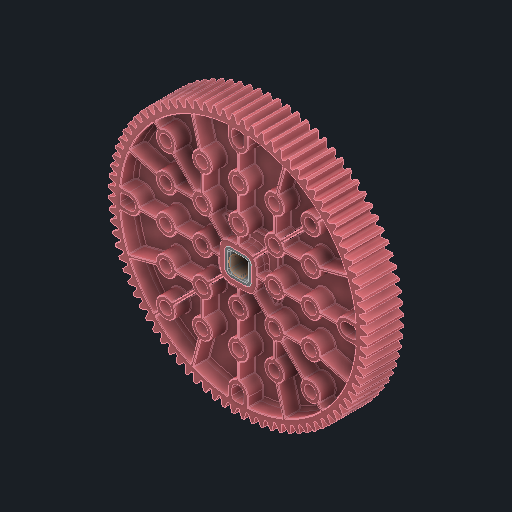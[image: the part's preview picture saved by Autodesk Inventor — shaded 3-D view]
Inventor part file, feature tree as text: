
AUTODESK INVENTOR PART (.ipt)
format: ipt  version: 2024 (Build 280153000, 153)  size: 5,321,216 bytes
history: native  units: in
note: dims shown in document units (in); Inventor stores cm internally (conversion verified against a paired STEP export)
features: other x3, extrude x1
ambient origin geometry x8: Origin, YZ Plane, XZ Plane, XY Plane, X Axis, Y Axis, Z Axis, Center Point
bodies: Solid1 (feature_tree), Solid2 (feature_tree)
feature tree (4):
  other  "Srf1"
  other  "276-7749-001_OVERMOLD Rev3_84T 24DP Gear Rev1_1:1"
  other  "276-7573-002 Rev7_2:1"
  extrude  "ExtrusionSrf1"  Depth=0.25in
